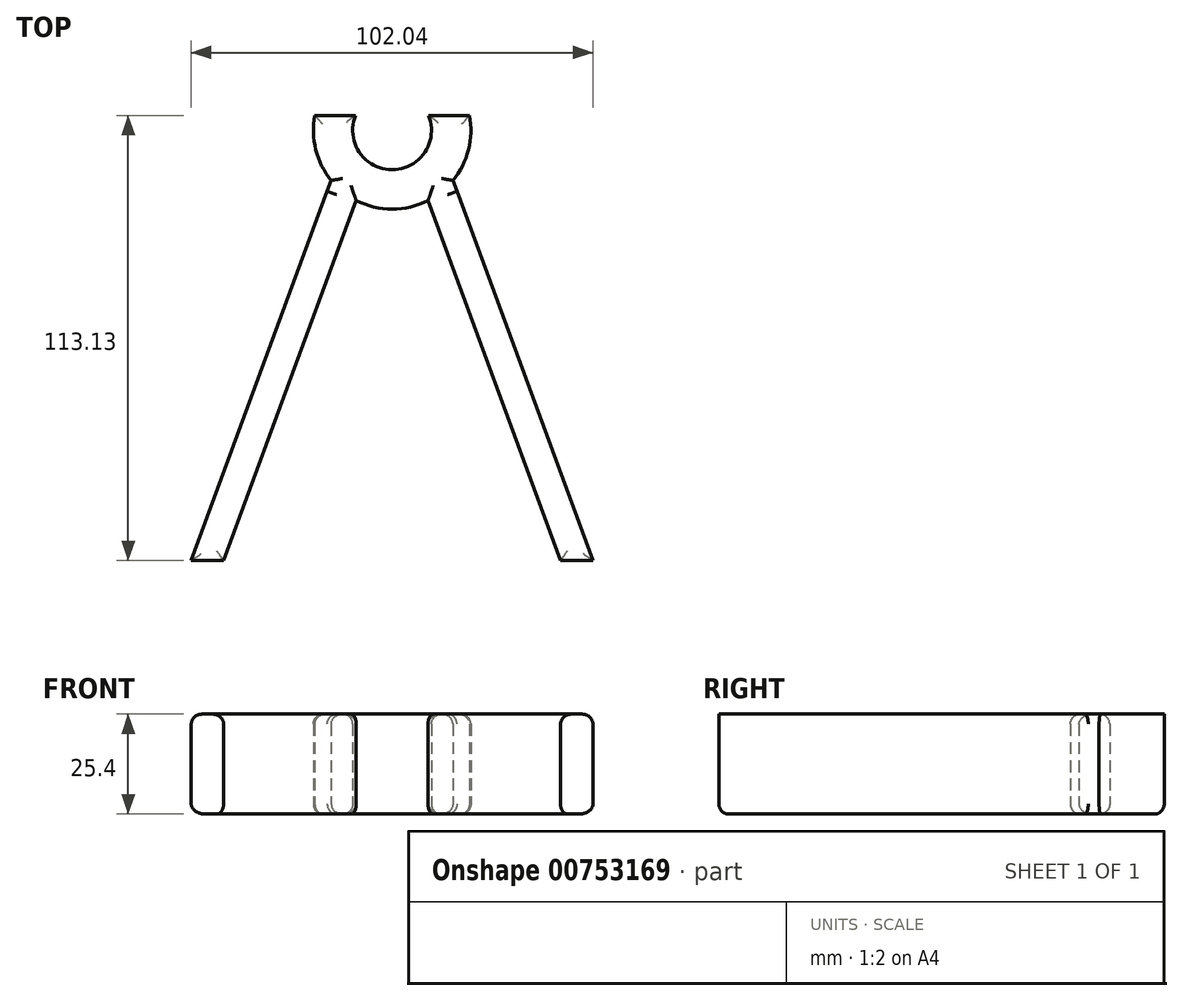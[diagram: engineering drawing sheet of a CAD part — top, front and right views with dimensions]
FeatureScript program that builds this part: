
annotation { "Feature Type Name" : "Feature", "Feature Type Description" : "" }
export const myFeature = defineFeature(function(context is Context, id is Id, definition is map)
    precondition{}
    {
        {
            var Q0;
            Q0=qCreatedBy(makeId("Top.planeOp"),FACE);
            var sketch = newSketch(context, id + "F0", { "sketchPlane" : qUnion([Q0])});
            skArc(sketch, "E0", {"start": v(-9.24, 3.83) * mm, "mid": v(0, -10) * mm, "end": v(9.24, 3.83) * mm});
            skArc(sketch, "E1.0", {"start": v(-19.63, 3.83) * mm, "mid": v(0, -20) * mm, "end": v(19.63, 3.83) * mm});
            skPoint(sketch, "E2", {"position": v(0, 3.83) * mm});
            skLineSegment(sketch, "E3", {"start": v(-19.63, 3.83) * mm, "end": v(-9.24, 3.83) * mm});
            skPoint(sketch, "E4.orphan", {"position": v(-24.85, 3.83) * mm});
            skLineSegment(sketch, "E5.trimOffspring", {"start": v(9.24, 3.83) * mm, "end": v(19.63, 3.83) * mm});
            skLineSegment(sketch, "E6", {"start": v(0, 0) * mm, "end": v(0, -31.32) * mm});
            skPoint(sketch, "E6.endSnap0", {"position": v(0, -10) * mm});
            skLineSegment(sketch, "E7", {"start": v(24.42, -59.37) * mm, "end": v(42.8, -109.3) * mm});
            skLineSegment(sketch, "E8", {"start": v(42.8, -109.3) * mm, "end": v(51.02, -109.3) * mm});
            skLineSegment(sketch, "E9", {"start": v(16.47, -15.46) * mm, "end": v(51.02, -109.3) * mm});
            skLineSegment(sketch, "E10", {"start": v(16.47, -15.46) * mm, "end": v(14, -8.88) * mm});
            skPoint(sketch, "E11.orphan", {"position": v(59.24, -109.3) * mm});
            skLineSegment(sketch, "E12", {"start": v(24.42, -59.37) * mm, "end": v(8.25, -15.46) * mm});
            skLineSegment(sketch, "E13.MirrorCS", {"start": v(-24.42, -59.37) * mm, "end": v(-8.25, -15.46) * mm});
            skLineSegment(sketch, "E14.MirrorCS", {"start": v(-16.47, -15.46) * mm, "end": v(-51.02, -109.3) * mm});
            skLineSegment(sketch, "E15.MirrorCS", {"start": v(-16.47, -15.46) * mm, "end": v(-14, -8.88) * mm});
            skLineSegment(sketch, "E16.MirrorCS", {"start": v(-24.42, -59.37) * mm, "end": v(-42.8, -109.3) * mm});
            skLineSegment(sketch, "E17.MirrorCS", {"start": v(-42.8, -109.3) * mm, "end": v(-51.02, -109.3) * mm});
            skLineSegment(sketch, "E18", {"start": v(51.02, -109.3) * mm, "end": v(-51.02, -109.3) * mm});
            skSolve(sketch);
        }
        {
            var Q0;
            {var subQ1=sQuery(id+"F0.wireOp",EDGE,"E14.MirrorCS");Q0=makeQuery(id+"F0.imprint","IMPRINT",FACE,{"disambiguationData":[TD([[makeQuery(id+"F0.imprint","IMPRINT",EDGE,{"derivedFrom":subQ1}),1.0]])]});}
            var Q1;
            {var subQ4=sQuery(id+"F0.wireOp",EDGE,"E7");Q1=makeQuery(id+"F0.imprint","IMPRINT",FACE,{"disambiguationData":[TD([[makeQuery(id+"F0.imprint","IMPRINT",EDGE,{"derivedFrom":subQ4}),1.0]])]});}
            var Q2;
            {var subQ0=sQuery(id+"F0.wireOp",EDGE,"E5.trimOffspring");Q2=makeQuery(id+"F0.imprint","IMPRINT",FACE,{"disambiguationData":[TD([[makeQuery(id+"F0.imprint","IMPRINT",EDGE,{"derivedFrom":subQ0}),-1.0]])]});}
            var Q3;
            {var subQ5=sQuery(id+"F0.wireOp",EDGE,"E3");Q3=makeQuery(id+"F0.imprint","IMPRINT",FACE,{"disambiguationData":[TD([[makeQuery(id+"F0.imprint","IMPRINT",EDGE,{"derivedFrom":subQ5}),-1.0]])]});}
            extrude(context, id + "F1", {"entities" : qUnion([Q0, Q1, Q2, Q3]), "depth" : 25.4 * mm, "offsetDistance" : 25.4 * mm});
        }
        {
            var Q0;
            Q0=makeQuery(id+"F1.opExtrude","CAP_EDGE",EDGE,{"disambiguationData":[OSD([sQuery(id+"F0.wireOp",EDGE,"E14.MirrorCS")])],"isStart":true});
            var Q1;
            Q1=makeQuery(id+"F1.opExtrude","CAP_EDGE",EDGE,{"disambiguationData":[OSD([sQuery(id+"F0.wireOp",EDGE,"E14.MirrorCS")])],"isStart":false});
            var Q2;
            Q2=makeQuery(id+"F1.opExtrude","CAP_EDGE",EDGE,{"disambiguationData":[OSD([sQuery(id+"F0.wireOp",EDGE,"E7"),sQuery(id+"F0.wireOp",EDGE,"E12")])],"isStart":false});
            var Q3;
            Q3=makeQuery(id+"F1.opExtrude","CAP_EDGE",EDGE,{"disambiguationData":[OSD([sQuery(id+"F0.wireOp",EDGE,"E9")])],"isStart":false});
            var Q4;
            Q4=makeQuery(id+"F1.opExtrude","CAP_EDGE",EDGE,{"disambiguationData":[OSD([sQuery(id+"F0.wireOp",EDGE,"E13.MirrorCS"),sQuery(id+"F0.wireOp",EDGE,"E16.MirrorCS")])],"isStart":false});
            var Q5;
            Q5=makeQuery(id+"F1.opExtrude","CAP_EDGE",EDGE,{"disambiguationData":[OSD([sQuery(id+"F0.wireOp",EDGE,"E7"),sQuery(id+"F0.wireOp",EDGE,"E12")])],"isStart":true});
            var Q6;
            Q6=makeQuery(id+"F1.opExtrude","CAP_EDGE",EDGE,{"disambiguationData":[OSD([sQuery(id+"F0.wireOp",EDGE,"E9")])],"isStart":true});
            var Q7;
            Q7=makeQuery(id+"F1.opExtrude","CAP_EDGE",EDGE,{"disambiguationData":[OSD([sQuery(id+"F0.wireOp",EDGE,"E13.MirrorCS"),sQuery(id+"F0.wireOp",EDGE,"E16.MirrorCS")])],"isStart":true});
            var Q8;
            Q8=makeQuery(id+"F1.opExtrude","CAP_EDGE",EDGE,{"disambiguationData":[OSD([sQuery(id+"F0.wireOp",EDGE,"E10")])],"isStart":false});
            var Q9;
            Q9=makeQuery(id+"F1.opExtrude","CAP_EDGE",EDGE,{"disambiguationData":[OSD([sQuery(id+"F0.wireOp",EDGE,"E10")])],"isStart":true});
            var Q10;
            Q10=makeQuery(id+"F1.opExtrude","CAP_EDGE",EDGE,{"disambiguationData":[OSD([sQuery(id+"F0.wireOp",EDGE,"E15.MirrorCS")])],"isStart":false});
            var Q11;
            Q11=makeQuery(id+"F1.opExtrude","CAP_EDGE",EDGE,{"disambiguationData":[OSD([sQuery(id+"F0.wireOp",EDGE,"E15.MirrorCS")])],"isStart":true});
            var Q12;
            {var subQ0=sQuery(id+"F0.wireOp",EDGE,"E1.0");var subQ1=makeQuery(id+"F0.imprint","INTERSECT",VERTEX,{"derivedFrom":[subQ0,sQuery(id+"F0.wireOp",EDGE,"E6")]});Q12=makeQuery(id+"F1.opExtrude","CAP_EDGE",EDGE,{"disambiguationData":[OSD([subQ0]),TDD([makeQuery(id+"F0.imprint","IMPRINT",EDGE,{"disambiguationData":[TD([[makeQuery(id+"F0.imprint","INTERSECT",VERTEX,{"derivedFrom":[subQ0,sQuery(id+"F0.wireOp",EDGE,"E13.MirrorCS")]}),-1.0]])],"derivedFrom":subQ0}),makeQuery(id+"F0.imprint","IMPRINT",EDGE,{"disambiguationData":[TD([[subQ1,-1.0]])],"derivedFrom":subQ0})])],"isStart":false});}
            var Q13;
            {var subQ0=sQuery(id+"F0.wireOp",EDGE,"E1.0");Q13=makeQuery(id+"F1.opExtrude","CAP_EDGE",EDGE,{"disambiguationData":[OSD([subQ0]),TDD([makeQuery(id+"F0.imprint","IMPRINT",EDGE,{"disambiguationData":[TD([[makeQuery(id+"F0.imprint","INTERSECT",VERTEX,{"derivedFrom":[subQ0,sQuery(id+"F0.wireOp",EDGE,"E3")]}),-1.0]])],"derivedFrom":subQ0})])],"isStart":false});}
            var Q14;
            {var subQ0=sQuery(id+"F0.wireOp",EDGE,"E1.0");Q14=makeQuery(id+"F1.opExtrude","CAP_EDGE",EDGE,{"disambiguationData":[OSD([subQ0]),TDD([makeQuery(id+"F0.imprint","IMPRINT",EDGE,{"disambiguationData":[TD([[makeQuery(id+"F0.imprint","INTERSECT",VERTEX,{"derivedFrom":[subQ0,sQuery(id+"F0.wireOp",EDGE,"E5.trimOffspring")]}),1.0]])],"derivedFrom":subQ0})])],"isStart":false});}
            var Q15;
            {var subQ0=sQuery(id+"F0.wireOp",EDGE,"E1.0");Q15=makeQuery(id+"F1.opExtrude","CAP_EDGE",EDGE,{"disambiguationData":[OSD([subQ0]),TDD([makeQuery(id+"F0.imprint","IMPRINT",EDGE,{"disambiguationData":[TD([[makeQuery(id+"F0.imprint","INTERSECT",VERTEX,{"derivedFrom":[subQ0,sQuery(id+"F0.wireOp",EDGE,"E5.trimOffspring")]}),1.0]])],"derivedFrom":subQ0})])],"isStart":true});}
            var Q16;
            Q16=makeQuery(id+"F1.opExtrude","CAP_FACE",FACE,{"disambiguationData":[OSD([sQuery(id+"F0.wireOp",EDGE,"E0"),sQuery(id+"F0.wireOp",EDGE,"E1.0"),sQuery(id+"F0.wireOp",EDGE,"E3"),sQuery(id+"F0.wireOp",EDGE,"E5.trimOffspring"),sQuery(id+"F0.wireOp",EDGE,"E7"),sQuery(id+"F0.wireOp",EDGE,"E9"),sQuery(id+"F0.wireOp",EDGE,"E10"),sQuery(id+"F0.wireOp",EDGE,"E12"),sQuery(id+"F0.wireOp",EDGE,"E13.MirrorCS"),sQuery(id+"F0.wireOp",EDGE,"E14.MirrorCS"),sQuery(id+"F0.wireOp",EDGE,"E15.MirrorCS"),sQuery(id+"F0.wireOp",EDGE,"E16.MirrorCS"),sQuery(id+"F0.wireOp",EDGE,"E18")])],"isStart":true});
            var Q17;
            Q17=makeQuery(id+"F1.opExtrude","CAP_EDGE",EDGE,{"disambiguationData":[OSD([sQuery(id+"F0.wireOp",EDGE,"E0")])],"isStart":true});
            var Q18;
            Q18=makeQuery(id+"F1.opExtrude","CAP_EDGE",EDGE,{"disambiguationData":[OSD([sQuery(id+"F0.wireOp",EDGE,"E0")])],"isStart":false});
            fillet(context, id + "F2", {"entities" : qUnion([Q0, Q1, Q2, Q3, Q4, Q5, Q6, Q7, Q8, Q9, Q10, Q11, Q12, Q13, Q14, Q15, Q16, Q17, Q18]), "radius" : 2.54 * mm, "tangentPropagation" : true, "allowEdgeOverflow" : false});
        }
    });
